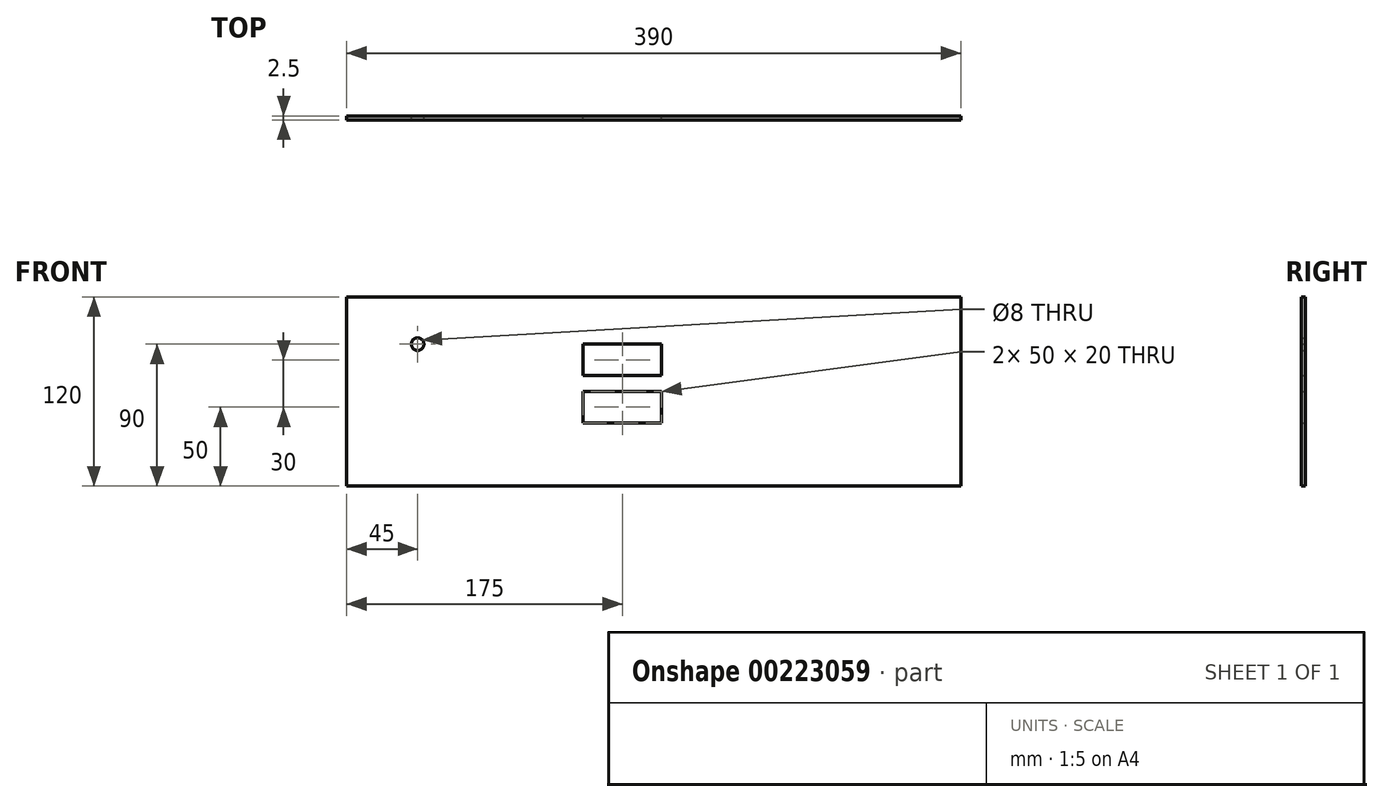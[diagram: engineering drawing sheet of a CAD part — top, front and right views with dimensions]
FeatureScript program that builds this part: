
annotation { "Feature Type Name" : "Feature", "Feature Type Description" : "" }
export const myFeature = defineFeature(function(context is Context, id is Id, definition is map)
    precondition{}
    {
        {
            var Q0;
            Q0=qCreatedBy(makeId("Front.planeOp"),FACE);
            var sketch = newSketch(context, id + "F0", { "sketchPlane" : qUnion([Q0])});
            skLineSegment(sketch, "E0.bottom", {"start": v(195, -60) * mm, "end": v(-195, -60) * mm});
            skLineSegment(sketch, "E0.top", {"start": v(195, 60) * mm, "end": v(-195, 60) * mm});
            skLineSegment(sketch, "E0.left", {"start": v(195, -60) * mm, "end": v(195, 60) * mm});
            skLineSegment(sketch, "E0.right", {"start": v(-195, -60) * mm, "end": v(-195, 60) * mm});
            skPoint(sketch, "E0.middle", {"position": v(0, 0) * mm});
            skLineSegment(sketch, "E1.bottom", {"start": v(-45, 30) * mm, "end": v(5, 30) * mm});
            skLineSegment(sketch, "E1.top", {"start": v(-45, 10) * mm, "end": v(5, 10) * mm});
            skLineSegment(sketch, "E1.left", {"start": v(-45, 30) * mm, "end": v(-45, 10) * mm});
            skLineSegment(sketch, "E1.right", {"start": v(5, 30) * mm, "end": v(5, 10) * mm});
            skLineSegment(sketch, "E2", {"start": v(-45, 52.44) * mm, "end": v(-45, -91.22) * mm, "construction": true});
            skLineSegment(sketch, "E3", {"start": v(-27.13, 30) * mm, "end": v(-234.1, 30) * mm, "construction": true});
            skLineSegment(sketch, "E4.bottom", {"start": v(-45, 0) * mm, "end": v(5, 0) * mm});
            skLineSegment(sketch, "E4.top", {"start": v(-45, -20) * mm, "end": v(5, -20) * mm});
            skLineSegment(sketch, "E4.left", {"start": v(-45, 0) * mm, "end": v(-45, -20) * mm});
            skLineSegment(sketch, "E4.right", {"start": v(5, 0) * mm, "end": v(5, -20) * mm});
            skCircle(sketch, "E5", {"center": v(-150, 30) * mm, "radius": 4 * mm});
            skSolve(sketch);
        }
        {
            var Q0;
            Q0=makeQuery(id+"F0.imprint","IMPRINT",FACE,{"disambiguationData":[TD([[makeQuery(id+"F0.imprint","IMPRINT",EDGE,{"derivedFrom":sQuery(id+"F0.wireOp",EDGE,"E0.bottom")}),-1.0]])]});
            extrude(context, id + "F1", {"entities" : qUnion([Q0]), "depth" : 2.5 * mm});
        }
    });
